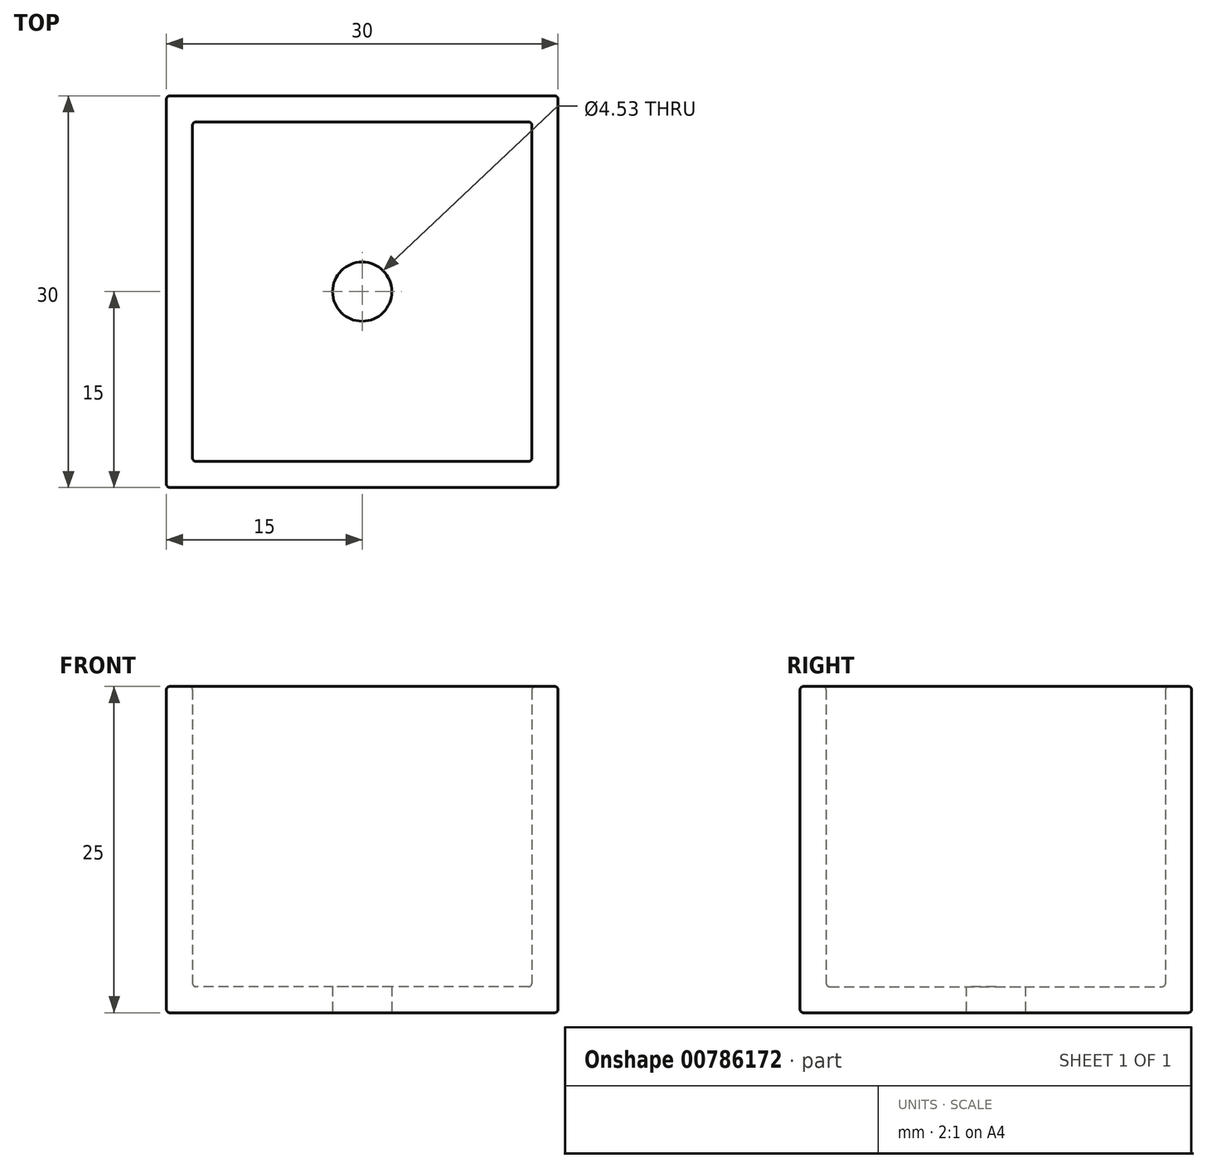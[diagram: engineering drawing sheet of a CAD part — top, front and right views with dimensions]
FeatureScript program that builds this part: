
annotation { "Feature Type Name" : "Feature", "Feature Type Description" : "" }
export const myFeature = defineFeature(function(context is Context, id is Id, definition is map)
    precondition{}
    {
        {
            var Q0;
            Q0=qCreatedBy(makeId("Top.planeOp"),FACE);
            var sketch = newSketch(context, id + "F0", { "sketchPlane" : qUnion([Q0])});
            skLineSegment(sketch, "E0.bottom", {"start": v(15, -15) * mm, "end": v(-15, -15) * mm});
            skLineSegment(sketch, "E0.top", {"start": v(15, 15) * mm, "end": v(-15, 15) * mm});
            skLineSegment(sketch, "E0.left", {"start": v(15, -15) * mm, "end": v(15, 15) * mm});
            skLineSegment(sketch, "E0.right", {"start": v(-15, -15) * mm, "end": v(-15, 15) * mm});
            skPoint(sketch, "E0.middle", {"position": v(0, 0) * mm});
            skSolve(sketch);
        }
        {
            var Q0;
            Q0=makeQuery(id+"F0.imprint","IMPRINT",FACE,{"disambiguationData":[TD([[makeQuery(id+"F0.imprint","IMPRINT",EDGE,{"derivedFrom":sQuery(id+"F0.wireOp",EDGE,"E0.bottom")}),-1.0]])]});
            extrude(context, id + "F1", {"entities" : qUnion([Q0]), "depth" : 25 * mm, "offsetDistance" : 25 * mm});
        }
        {
            var Q0;
            Q0=makeQuery(id+"F1.opExtrude","CAP_FACE",FACE,{"disambiguationData":[OSD([sQuery(id+"F0.wireOp",EDGE,"E0.bottom"),sQuery(id+"F0.wireOp",EDGE,"E0.top"),sQuery(id+"F0.wireOp",EDGE,"E0.left"),sQuery(id+"F0.wireOp",EDGE,"E0.right")])],"isStart":false});
            shell(context, id + "F2", {"entities" : qUnion([Q0]), "thickness" : 2 * mm});
        }
        {
            var Q0;
            Q0=makeQuery(id+"F2.opShell","OFFSET_FACE",FACE,{"disambiguationData":[OSD([sQuery(id+"F0.wireOp",EDGE,"E0.top")])]});
            var Q1;
            Q1=makeQuery(id+"F2.opShell","OFFSET_FACE",FACE,{"disambiguationData":[OSD([sQuery(id+"F0.wireOp",EDGE,"E0.right")])]});
            var Q2;
            Q2=makeQuery(id+"F2.opShell","OFFSET_FACE",FACE,{"disambiguationData":[OSD([sQuery(id+"F0.wireOp",EDGE,"E0.bottom")])]});
            var Q3;
            Q3=makeQuery(id+"F2.opShell","OFFSET_FACE",FACE,{"disambiguationData":[OSD([sQuery(id+"F0.wireOp",EDGE,"E0.left")])]});
            var Q4;
            Q4=makeQuery(id+"F1.opExtrude","CAP_FACE",FACE,{"disambiguationData":[OSD([sQuery(id+"F0.wireOp",EDGE,"E0.bottom"),sQuery(id+"F0.wireOp",EDGE,"E0.top"),sQuery(id+"F0.wireOp",EDGE,"E0.left"),sQuery(id+"F0.wireOp",EDGE,"E0.right")])],"isStart":true});
            var Q5;
            Q5=makeQuery(id+"F1.opExtrude","SWEPT_FACE",FACE,{"disambiguationData":[OSD([sQuery(id+"F0.wireOp",EDGE,"E0.bottom")])]});
            var Q6;
            Q6=makeQuery(id+"F1.opExtrude","SWEPT_FACE",FACE,{"disambiguationData":[OSD([sQuery(id+"F0.wireOp",EDGE,"E0.top")])]});
            var Q7;
            Q7=makeQuery(id+"F1.opExtrude","SWEPT_FACE",FACE,{"disambiguationData":[OSD([sQuery(id+"F0.wireOp",EDGE,"E0.right")])]});
            var Q8;
            Q8=makeQuery(id+"F1.opExtrude","SWEPT_FACE",FACE,{"disambiguationData":[OSD([sQuery(id+"F0.wireOp",EDGE,"E0.left")])]});
            fillet(context, id + "F3", {"entities" : qUnion([Q0, Q1, Q2, Q3, Q4, Q5, Q6, Q7, Q8]), "radius" : 0.25 * mm, "tangentPropagation" : true, "allowEdgeOverflow" : false});
        }
        {
            var Q0;
            Q0=makeQuery(id+"F1.opExtrude","CAP_FACE",FACE,{"disambiguationData":[OSD([sQuery(id+"F0.wireOp",EDGE,"E0.bottom"),sQuery(id+"F0.wireOp",EDGE,"E0.top"),sQuery(id+"F0.wireOp",EDGE,"E0.left"),sQuery(id+"F0.wireOp",EDGE,"E0.right")])],"isStart":true});
            var sketch = newSketch(context, id + "F4", { "sketchPlane" : qUnion([Q0])});
            skCircle(sketch, "E1", {"center": v(0, 0) * mm, "radius": 2.27 * mm});
            skSolve(sketch);
        }
        {
            var Q0;
            Q0=makeQuery(id+"F4.imprint","IMPRINT",FACE,{"disambiguationData":[TD([[makeQuery(id+"F4.imprint","IMPRINT",EDGE,{"derivedFrom":sQuery(id+"F4.wireOp",EDGE,"E1")}),1.0]])]});
            extrude(context, id + "F5", {"entities" : qUnion([Q0]), "operationType" : NewBodyOperationType.REMOVE, "endBound" : BoundingType.THROUGH_ALL, "oppositeDirection" : true, "depth" : 25 * mm, "offsetDistance" : 25 * mm});
        }
    });
